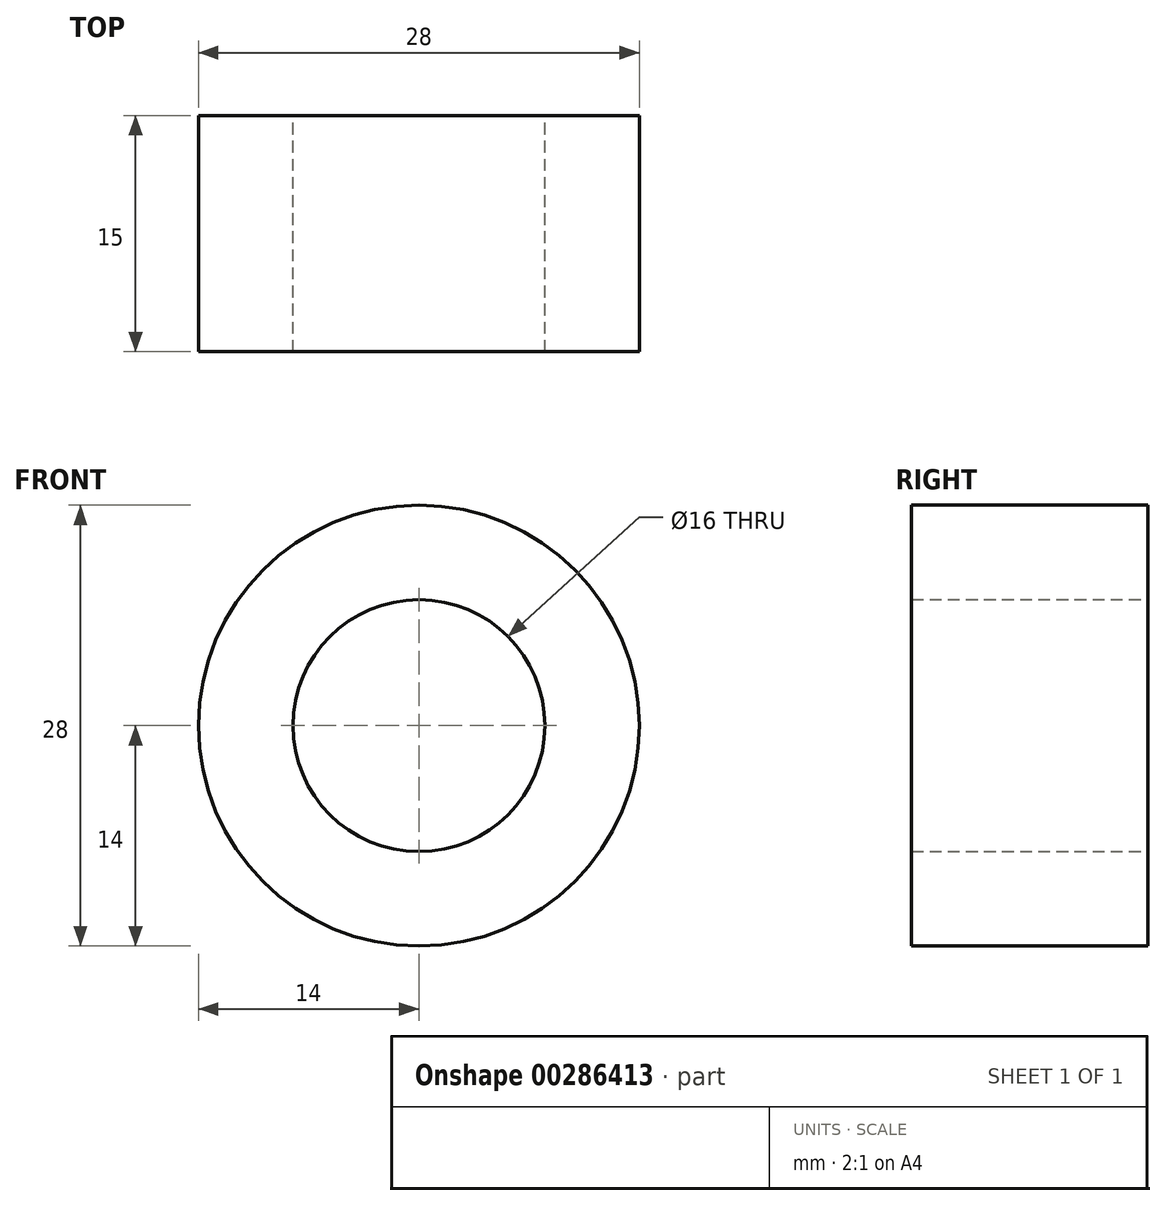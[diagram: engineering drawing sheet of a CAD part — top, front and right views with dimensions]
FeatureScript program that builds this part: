
annotation { "Feature Type Name" : "Feature", "Feature Type Description" : "" }
export const myFeature = defineFeature(function(context is Context, id is Id, definition is map)
    precondition{}
    {
        {
            var Q0;
            Q0=qCreatedBy(makeId("Front.planeOp"),FACE);
            var sketch = newSketch(context, id + "F0", { "sketchPlane" : qUnion([Q0])});
            skCircle(sketch, "E0", {"center": v(0, 0) * mm, "radius": 14 * mm});
            skCircle(sketch, "E1", {"center": v(0, 0) * mm, "radius": 8 * mm});
            skSolve(sketch);
        }
        {
            var Q0;
            Q0 = qSketchRegion(id + "F0", true);
            extrude(context, id + "F1", {"entities" : qUnion([Q0]), "depth" : 15 * mm});
        }
    });
